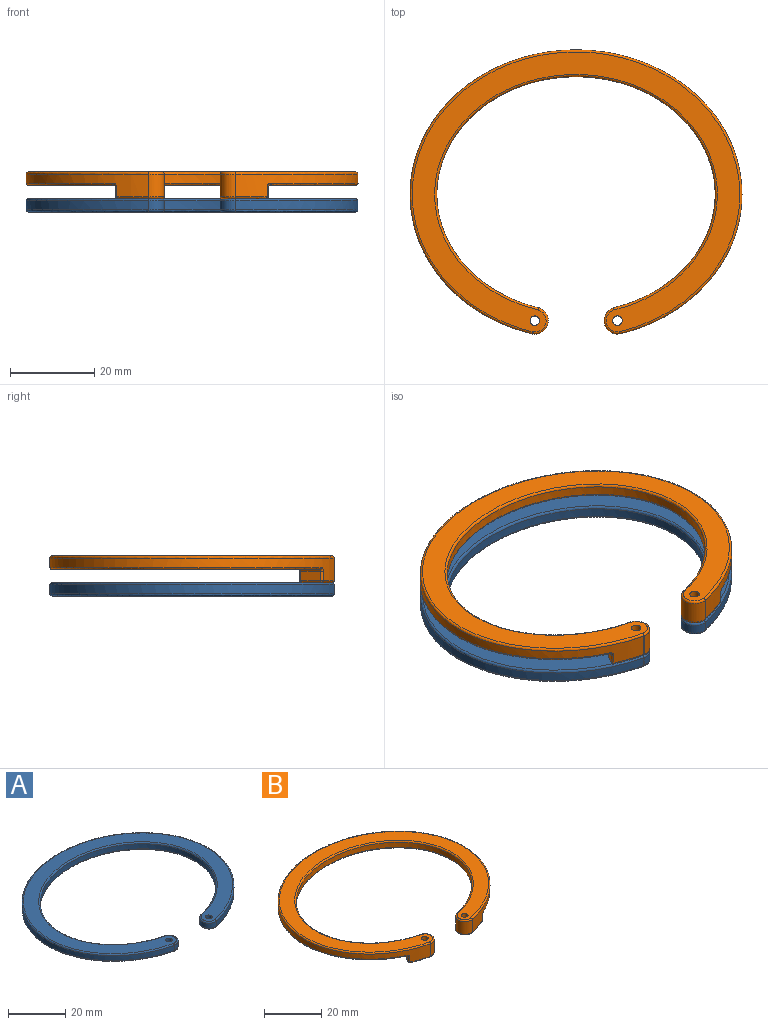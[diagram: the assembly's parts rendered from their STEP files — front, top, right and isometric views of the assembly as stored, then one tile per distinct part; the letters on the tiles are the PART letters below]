
ASSEMBLY  parts=2 mates=1
PART A: 28 faces, bbox 78.8x68.2x3.2 mm
  f0: cylinder r=3.18mm len=6.2mm, axis (0,0,-1), area 20.4mm2, adj f13,f22,f23,f27
  f1: extruded ~78.65x67.39mm, area 455.2mm2, adj f8,f12,f13,f14
  f2: cylinder r=3.18mm len=6.2mm, axis (0,0,-1), area 20.4mm2, adj f8,f11,f15,f16
  f3: extruded ~65.98x54.87mm, area 375.7mm2, adj f16,f21,f24,f27
  f4: plane 77.73x66.42mm, normal (0,0,1), area 1036.2mm2, adj f6,f7,f11,f12,f21,f22
  f5: plane 77.74x66.42mm, normal (0,0,-1), area 1037.2mm2, adj f6,f7,f14,f15,f23,f24
  f6: cylinder r=1.13mm len=3.18mm, axis (0,0,1), area 22.5mm2, adj f4,f5
  f7: cylinder r=1.13mm len=3.18mm, axis (0,0,1), area 22.5mm2, adj f4,f5
  f8: cylinder r=0.51mm len=2.16mm, axis (0,0,-1), area 0.1mm2, adj f1,f2,f9,f10
  f9: sphere r=0.51mm, area 0mm2, adj f8,f11,f12
  f10: sphere r=0.51mm, area 0mm2, adj f8,f14,f15
  f11: torus R=2.67mm, axis (0,0,1), area 7.1mm2, adj f2,f4,f9,f17
  f12: bspline ~78.75x68.17mm, area 167.4mm2, adj f1,f4,f9,f18
  f13: cylinder r=0.51mm len=2.16mm, axis (0,0,-1), area 0.1mm2, adj f0,f1,f18,f19
  f14: bspline ~78.75x68.16mm, area 167.4mm2, adj f1,f5,f10,f19
  f15: torus R=2.67mm, axis (0,0,1), area 7.1mm2, adj f2,f5,f10,f20
  f16: cylinder r=0.51mm len=2.16mm, axis (0,0,-1), area 0.1mm2, adj f2,f3,f17,f20
  f17: sphere r=0.51mm, area 0mm2, adj f11,f16,f21
  f18: sphere r=0.51mm, area 0mm2, adj f12,f13,f22
  f19: sphere r=0.51mm, area 0mm2, adj f13,f14,f23
  f20: sphere r=0.51mm, area 0mm2, adj f15,f16,f24
  f21: bspline ~67.07x56.28mm, area 139.7mm2, adj f3,f4,f17,f25
  f22: torus R=2.67mm, axis (0,0,1), area 7.1mm2, adj f0,f4,f18,f25
  f23: torus R=2.67mm, axis (0,0,1), area 7.1mm2, adj f0,f5,f19,f26
  f24: bspline ~67.07x56.27mm, area 139.7mm2, adj f3,f5,f20,f26
  f25: sphere r=0.51mm, area 0mm2, adj f21,f22,f27
  f26: sphere r=0.51mm, area 0mm2, adj f23,f24,f27
  f27: cylinder r=0.51mm len=2.16mm, axis (0,0,-1), area 0.1mm2, adj f0,f3,f25,f26
PART B: 52 faces, bbox 78.8x68.2x6.4 mm
  f0: extruded ~65.98x54.87mm, area 415mm2, adj f10,f13,f17,f22,f27,f31,f32,f37
  f1: extruded ~78.65x67.39mm, area 506mm2, adj f15,f24,f25,f34,f35,f41,f44,f45
  f2: plane 77.73x63.47mm, normal (0,0,-1), area 939.1mm2, adj f36,f37,f45,f46
  f3: cylinder r=3.18mm len=6.2mm, axis (0,0,-1), area 50.4mm2, adj f10,f14,f15,f16
  f4: cylinder r=3.18mm len=6.2mm, axis (0,0,-1), area 50.4mm2, adj f22,f23,f33,f34
  f5: plane 77.73x66.42mm, normal (0,0,1), area 1036.2mm2, adj f13,f14,f23,f24,f50,f51
  f6: plane 4.6x2.78mm, normal (-0.86,0.52,0), area 11.6mm2, adj f26,f27,f35,f36
  f7: plane 10.53x7.13mm, normal (0,0,-1), area 43.5mm2, adj f16,f17,f25,f26,f50
  f8: plane 4.6x2.78mm, normal (0.86,0.52,0), area 11.6mm2, adj f38,f43,f46,f49
  f9: plane 10.47x7.11mm, normal (0,0,-1), area 43.2mm2, adj f32,f33,f43,f44,f51
  f10: cylinder r=0.51mm len=5.33mm, axis (0,0,-1), area 0.3mm2, adj f0,f3,f11,f12
  f11: sphere r=0.51mm, area 0mm2, adj f10,f13,f14
  f12: sphere r=0.51mm, area 0mm2, adj f10,f16,f17
  f13: bspline ~67.07x56.28mm, area 139.7mm2, adj f0,f5,f11,f18
  f14: torus R=2.67mm, axis (0,0,1), area 7.1mm2, adj f3,f5,f11,f19
  f15: cylinder r=0.51mm len=5.33mm, axis (0,0,-1), area 0.2mm2, adj f1,f3,f19,f20
  f16: torus R=2.67mm, axis (0,0,1), area 7.1mm2, adj f3,f7,f12,f20
  f17: bspline ~8.13x3.05mm, area 4.9mm2, adj f0,f7,f12,f21
  f18: sphere r=0.51mm, area 0mm2, adj f13,f22,f23
  f19: sphere r=0.51mm, area 0mm2, adj f14,f15,f24
  f20: sphere r=0.51mm, area 0mm2, adj f15,f16,f25
  f21: sphere r=0.51mm, area 0.4mm2, adj f17,f26,f27
  f22: cylinder r=0.51mm len=5.33mm, axis (0,0,-1), area 0.3mm2, adj f0,f4,f18,f28
  f23: torus R=2.67mm, axis (0,0,1), area 7.1mm2, adj f4,f5,f18,f29
  f24: bspline ~78.75x68.17mm, area 167.4mm2, adj f1,f5,f19,f29
  f25: bspline ~13.63x4.54mm, area 6.3mm2, adj f1,f7,f20,f30
  f26: cylinder r=0.51mm len=4.86mm, axis (0.52,0.86,0), area 4.3mm2, adj f6,f7,f21,f30
  f27: cylinder r=0.51mm len=2.16mm, axis (0,0,-1), area 1.6mm2, adj f0,f6,f21,f31
  f28: sphere r=0.51mm, area 0mm2, adj f22,f32,f33
  f29: sphere r=0.51mm, area 0mm2, adj f23,f24,f34
  f30: sphere r=0.51mm, area 0.4mm2, adj f25,f26,f35
  f31: bspline ~1.24x1.22mm, area 0.8mm2, adj f0,f27,f36,f37
  f32: bspline ~11.9x4.17mm, area 4.9mm2, adj f0,f9,f28,f39
  f33: torus R=2.67mm, axis (0,0,1), area 7.1mm2, adj f4,f9,f28,f40
  f34: cylinder r=0.51mm len=5.33mm, axis (0,0,-1), area 0.2mm2, adj f1,f4,f29,f40
  f35: cylinder r=0.51mm len=2.16mm, axis (0,0,-1), area 1.9mm2, adj f1,f6,f30,f41
  f36: cylinder r=0.51mm len=4.96mm, axis (-0.52,-0.86,0), area 4.3mm2, adj f2,f6,f31,f41
  f37: bspline ~67.07x54.32mm, area 128.3mm2, adj f0,f2,f31,f42
  f38: cylinder r=0.51mm len=2.16mm, axis (0,0,-1), area 1.6mm2, adj f0,f8,f39,f42
  f39: sphere r=0.51mm, area 0.4mm2, adj f32,f38,f43
  f40: sphere r=0.51mm, area 0mm2, adj f33,f34,f44
  f41: bspline ~1.2x1.15mm, area 0.9mm2, adj f1,f35,f36,f45
  f42: bspline ~1.25x1.2mm, area 0.8mm2, adj f0,f37,f38,f46
  f43: cylinder r=0.51mm len=4.86mm, axis (0.52,-0.86,0), area 4.3mm2, adj f8,f9,f39,f47
  f44: bspline ~12.29x4.23mm, area 6.3mm2, adj f1,f9,f40,f47
  f45: bspline ~78.75x65.78mm, area 153.2mm2, adj f1,f2,f41,f48
  f46: cylinder r=0.51mm len=4.96mm, axis (-0.52,0.86,0), area 4.3mm2, adj f2,f8,f42,f48
  f47: sphere r=0.51mm, area 0.4mm2, adj f43,f44,f49
  f48: bspline ~1.24x1.1mm, area 0.9mm2, adj f1,f45,f46,f49
  f49: cylinder r=0.51mm len=2.16mm, axis (0,0,-1), area 1.9mm2, adj f1,f8,f47,f48
  f50: cylinder r=1.13mm len=6.35mm, axis (0,0,1), area 45.1mm2, adj f5,f7
  f51: cylinder r=1.13mm len=6.35mm, axis (0,0,1), area 45.1mm2, adj f5,f9
PLACE A t=(-2.87,-5.13,-5.89)mm
PLACE B t=(-2.87,-5.13,0.46)mm
MATE revolute B.f50 <-> A.f6  axis (0,0,-1) through (-12.64,-35.09,-2.72)mm
